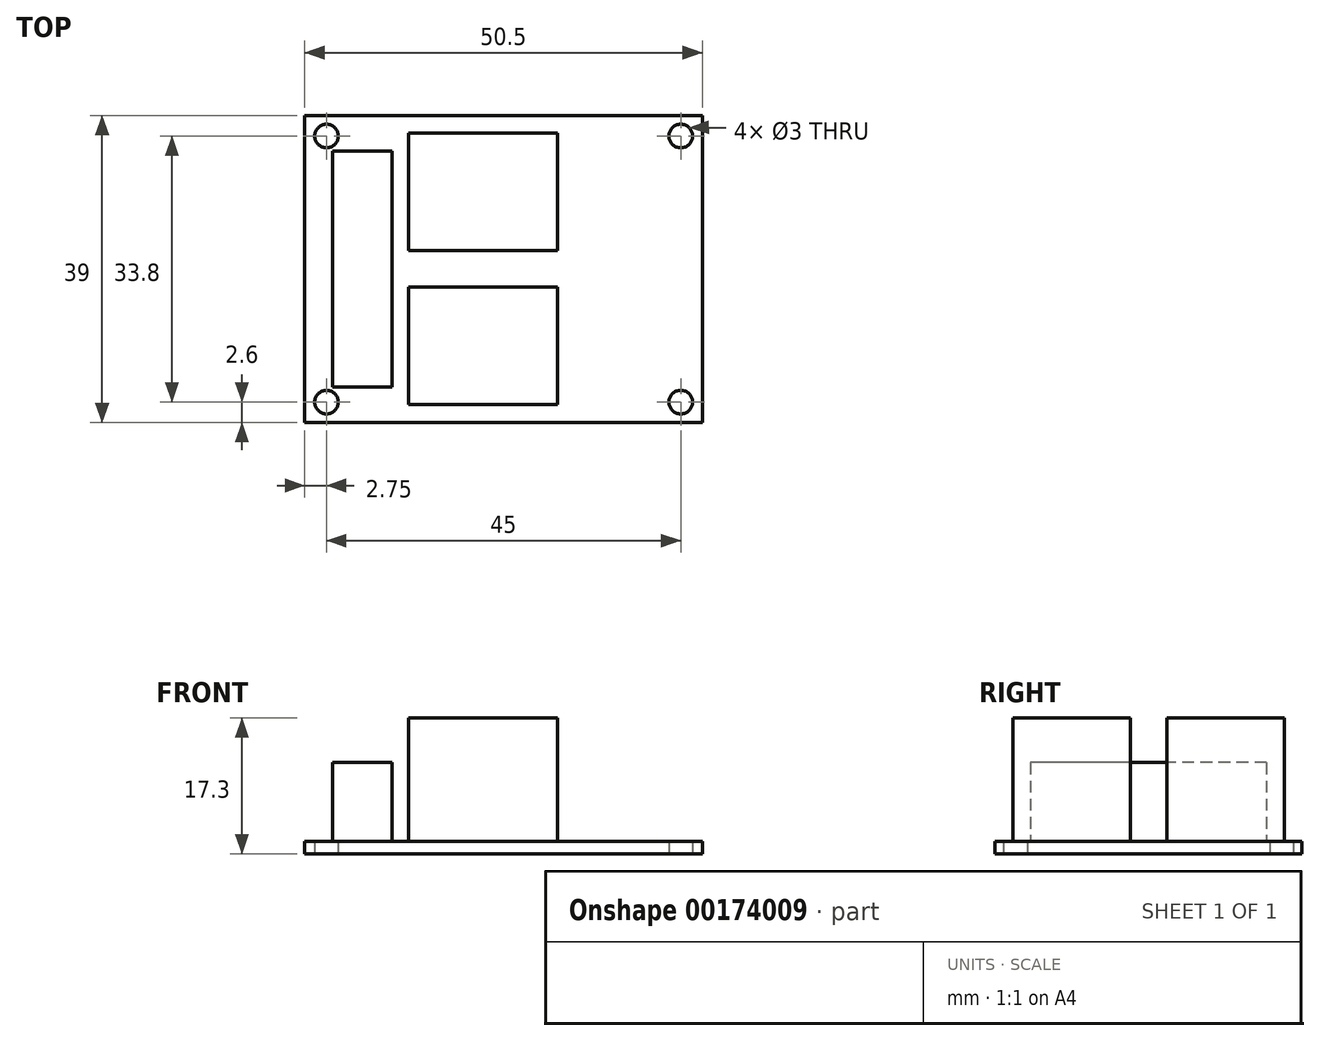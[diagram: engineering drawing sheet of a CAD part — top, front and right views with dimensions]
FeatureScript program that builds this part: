
annotation { "Feature Type Name" : "Feature", "Feature Type Description" : "" }
export const myFeature = defineFeature(function(context is Context, id is Id, definition is map)
    precondition{}
    {
        {
            var Q0;
            Q0=qCreatedBy(makeId("Top.planeOp"),FACE);
            var sketch = newSketch(context, id + "F0", { "sketchPlane" : qUnion([Q0])});
            skLineSegment(sketch, "E0.bottom", {"start": v(25.25, 19.5) * mm, "end": v(-25.25, 19.5) * mm});
            skLineSegment(sketch, "E0.top", {"start": v(25.25, -19.5) * mm, "end": v(-25.25, -19.5) * mm});
            skLineSegment(sketch, "E0.left", {"start": v(25.25, 19.5) * mm, "end": v(25.25, -19.5) * mm});
            skLineSegment(sketch, "E0.right", {"start": v(-25.25, 19.5) * mm, "end": v(-25.25, -19.5) * mm});
            skPoint(sketch, "E0.middle", {"position": v(0, 0) * mm});
            skLineSegment(sketch, "E1.bottom", {"start": v(22.5, 16.9) * mm, "end": v(-22.5, 16.9) * mm, "construction": true});
            skLineSegment(sketch, "E1.top", {"start": v(22.5, -16.9) * mm, "end": v(-22.5, -16.9) * mm, "construction": true});
            skLineSegment(sketch, "E1.left", {"start": v(22.5, 16.9) * mm, "end": v(22.5, -16.9) * mm, "construction": true});
            skLineSegment(sketch, "E1.right", {"start": v(-22.5, 16.9) * mm, "end": v(-22.5, -16.9) * mm, "construction": true});
            skCircle(sketch, "E2", {"center": v(-22.5, 16.9) * mm, "radius": 1.5 * mm});
            skCircle(sketch, "E3", {"center": v(22.5, 16.9) * mm, "radius": 1.5 * mm});
            skCircle(sketch, "E4", {"center": v(22.5, -16.9) * mm, "radius": 1.5 * mm});
            skCircle(sketch, "E5", {"center": v(-22.5, -16.9) * mm, "radius": 1.5 * mm});
            skSolve(sketch);
        }
        {
            var Q0;
            Q0 = qSketchRegion(id + "F0", true);
            extrude(context, id + "F1", {"entities" : qUnion([Q0]), "depth" : 1.6 * mm});
        }
        {
            var Q0;
            Q0=makeQuery(id+"F1.opExtrude","CAP_FACE",FACE,{"disambiguationData":[OSD([sQuery(id+"F0.wireOp",EDGE,"E0.bottom"),sQuery(id+"F0.wireOp",EDGE,"E0.top"),sQuery(id+"F0.wireOp",EDGE,"E0.left"),sQuery(id+"F0.wireOp",EDGE,"E0.right"),sQuery(id+"F0.wireOp",EDGE,"E2"),sQuery(id+"F0.wireOp",EDGE,"E3"),sQuery(id+"F0.wireOp",EDGE,"E4"),sQuery(id+"F0.wireOp",EDGE,"E5")])],"isStart":false});
            var sketch = newSketch(context, id + "F2", { "sketchPlane" : qUnion([Q0])});
            skLineSegment(sketch, "E6.bottom", {"start": v(6.85, 2.37) * mm, "end": v(-12.05, 2.37) * mm});
            skLineSegment(sketch, "E6.top", {"start": v(6.85, 17.27) * mm, "end": v(-12.05, 17.27) * mm});
            skLineSegment(sketch, "E6.left", {"start": v(6.85, 2.37) * mm, "end": v(6.85, 17.27) * mm});
            skLineSegment(sketch, "E6.right", {"start": v(-12.05, 2.37) * mm, "end": v(-12.05, 17.27) * mm});
            skPoint(sketch, "E6.middle", {"position": v(-2.6, 9.82) * mm});
            skLineSegment(sketch, "E7.bottom", {"start": v(6.85, -2.3) * mm, "end": v(-12.05, -2.3) * mm});
            skLineSegment(sketch, "E7.top", {"start": v(6.85, -17.2) * mm, "end": v(-12.05, -17.2) * mm});
            skLineSegment(sketch, "E7.left", {"start": v(6.85, -2.3) * mm, "end": v(6.85, -17.2) * mm});
            skLineSegment(sketch, "E7.right", {"start": v(-12.05, -2.3) * mm, "end": v(-12.05, -17.2) * mm});
            skPoint(sketch, "E7.middle", {"position": v(-2.6, -9.75) * mm});
            skSolve(sketch);
        }
        {
            var Q0;
            Q0 = qSketchRegion(id + "F2", true);
            extrude(context, id + "F3", {"entities" : qUnion([Q0]), "operationType" : NewBodyOperationType.ADD, "depth" : 15.7 * mm});
        }
        {
            var Q0;
            Q0=makeQuery(id+"F1.opExtrude","CAP_FACE",FACE,{"disambiguationData":[OSD([sQuery(id+"F0.wireOp",EDGE,"E0.bottom"),sQuery(id+"F0.wireOp",EDGE,"E0.top"),sQuery(id+"F0.wireOp",EDGE,"E0.left"),sQuery(id+"F0.wireOp",EDGE,"E0.right"),sQuery(id+"F0.wireOp",EDGE,"E2"),sQuery(id+"F0.wireOp",EDGE,"E3"),sQuery(id+"F0.wireOp",EDGE,"E4"),sQuery(id+"F0.wireOp",EDGE,"E5")])],"isStart":false});
            var sketch = newSketch(context, id + "F4", { "sketchPlane" : qUnion([Q0])});
            skLineSegment(sketch, "E8.bottom", {"start": v(-14.15, 15) * mm, "end": v(-21.75, 15) * mm});
            skLineSegment(sketch, "E8.top", {"start": v(-14.15, -15) * mm, "end": v(-21.75, -15) * mm});
            skLineSegment(sketch, "E8.left", {"start": v(-14.15, 15) * mm, "end": v(-14.15, -15) * mm});
            skLineSegment(sketch, "E8.right", {"start": v(-21.75, 15) * mm, "end": v(-21.75, -15) * mm});
            skPoint(sketch, "E8.middle", {"position": v(-17.95, 0) * mm});
            skSolve(sketch);
        }
        {
            var Q0;
            Q0 = qSketchRegion(id + "F4", true);
            extrude(context, id + "F5", {"entities" : qUnion([Q0]), "operationType" : NewBodyOperationType.ADD, "depth" : 10 * mm});
        }
    });
